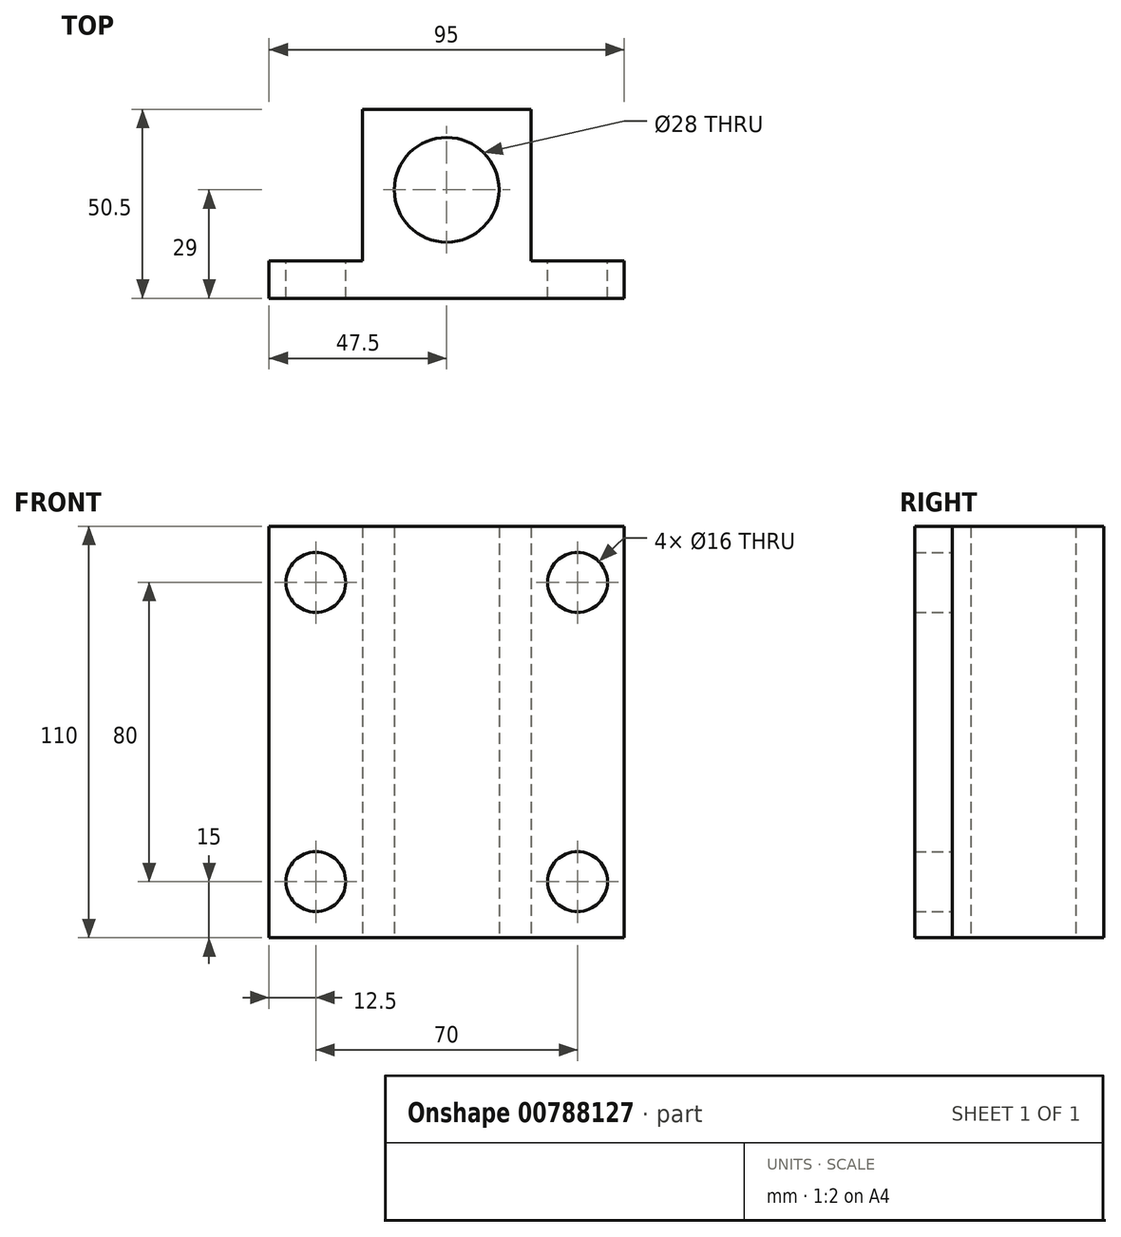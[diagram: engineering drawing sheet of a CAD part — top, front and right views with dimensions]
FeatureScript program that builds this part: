
annotation { "Feature Type Name" : "Feature", "Feature Type Description" : "" }
export const myFeature = defineFeature(function(context is Context, id is Id, definition is map)
    precondition{}
    {
        {
            var Q0;
            Q0=qCreatedBy(makeId("Top.planeOp"),FACE);
            var sketch = newSketch(context, id + "F0", { "sketchPlane" : qUnion([Q0])});
            skLineSegment(sketch, "E0", {"start": v(-47.5, 0) * mm, "end": v(-47.5, 10) * mm});
            skLineSegment(sketch, "E1", {"start": v(-47.5, 10) * mm, "end": v(-22.5, 10) * mm});
            skLineSegment(sketch, "E2", {"start": v(-22.5, 10) * mm, "end": v(-22.5, 50.5) * mm});
            skLineSegment(sketch, "E3", {"start": v(-22.5, 50.5) * mm, "end": v(22.5, 50.5) * mm});
            skLineSegment(sketch, "E4", {"start": v(22.5, 50.5) * mm, "end": v(22.5, 10) * mm});
            skLineSegment(sketch, "E5", {"start": v(22.5, 10) * mm, "end": v(47.5, 10) * mm});
            skLineSegment(sketch, "E6", {"start": v(47.5, 10) * mm, "end": v(47.5, 0) * mm});
            skLineSegment(sketch, "E7", {"start": v(47.5, 0) * mm, "end": v(-47.5, 0) * mm});
            skPoint(sketch, "E8", {"position": v(0, 0) * mm});
            skPoint(sketch, "E9", {"position": v(-35, 10) * mm});
            skPoint(sketch, "E10", {"position": v(35, 10) * mm});
            skCircle(sketch, "E11", {"center": v(0, 29) * mm, "radius": 14 * mm});
            skSolve(sketch);
        }
        {
            var Q0;
            Q0 = qSketchRegion(id + "F0", true);
            extrude(context, id + "F1", {"entities" : qUnion([Q0]), "depth" : 110 * mm, "offsetDistance" : 25 * mm});
        }
        {
            var Q0;
            Q0=makeQuery(id+"F1.opExtrude","SWEPT_FACE",FACE,{"disambiguationData":[OSD([sQuery(id+"F0.wireOp",EDGE,"E5")])]});
            var sketch = newSketch(context, id + "F2", { "sketchPlane" : qUnion([Q0])});
            skCircle(sketch, "E12", {"center": v(-35, 95) * mm, "radius": 8 * mm});
            skCircle(sketch, "E13", {"center": v(-35, 15) * mm, "radius": 8 * mm});
            skCircle(sketch, "E14", {"center": v(35, 95) * mm, "radius": 8 * mm});
            skCircle(sketch, "E15", {"center": v(35, 15) * mm, "radius": 8 * mm});
            skSolve(sketch);
        }
        {
            var Q0;
            Q0 = qSketchRegion(id + "F2", true);
            extrude(context, id + "F3", {"entities" : qUnion([Q0]), "operationType" : NewBodyOperationType.REMOVE, "oppositeDirection" : true, "depth" : 25 * mm, "offsetDistance" : 25 * mm});
        }
    });
